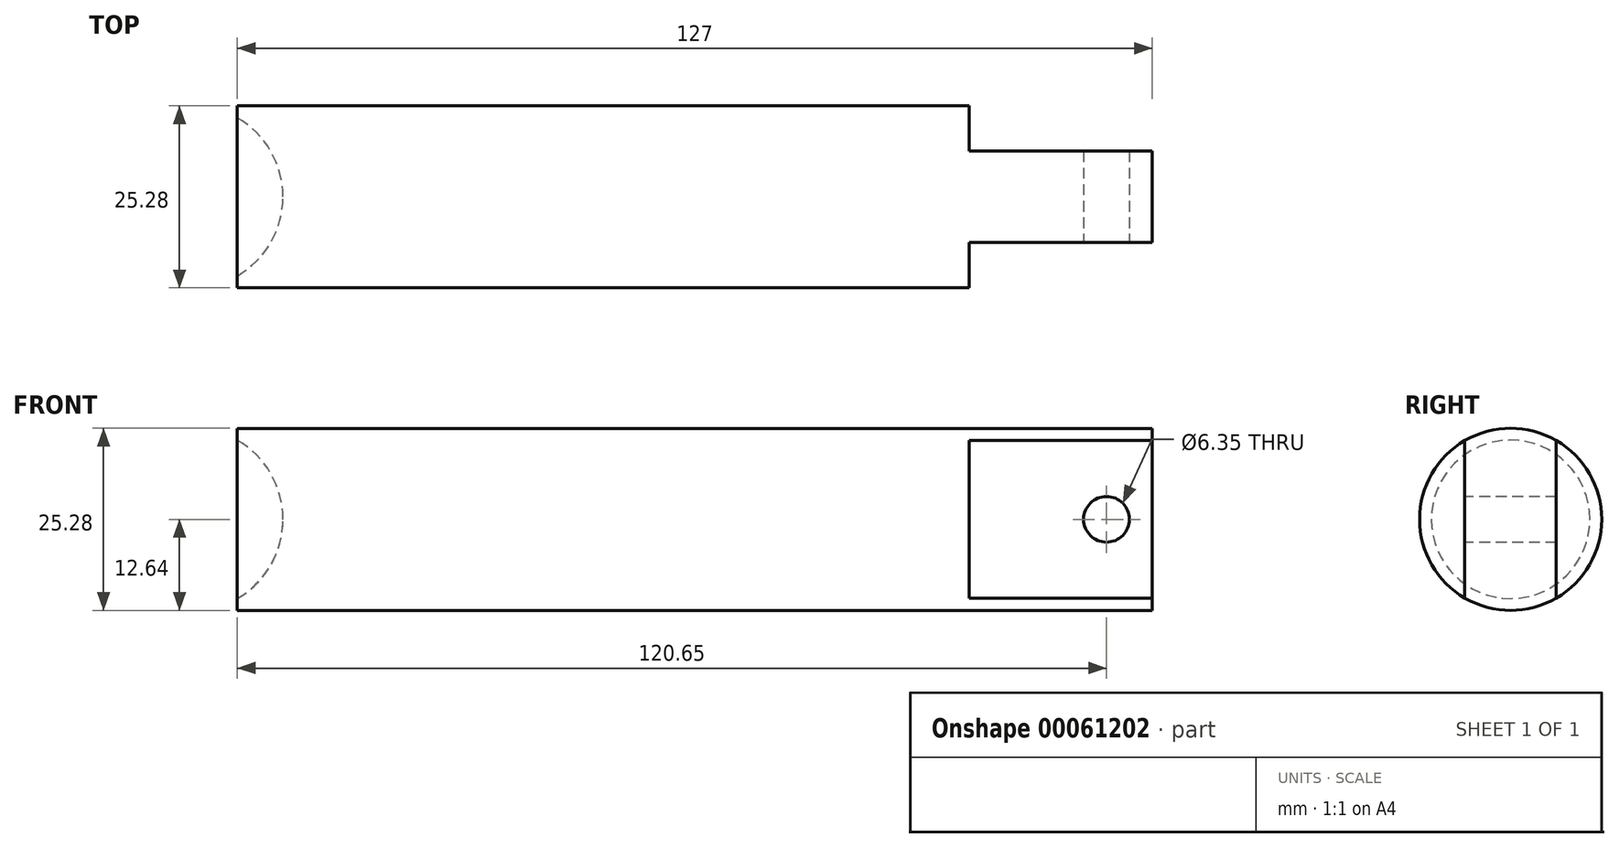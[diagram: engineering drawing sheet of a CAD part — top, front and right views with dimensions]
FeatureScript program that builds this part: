
annotation { "Feature Type Name" : "Feature", "Feature Type Description" : "" }
export const myFeature = defineFeature(function(context is Context, id is Id, definition is map)
    precondition{}
    {
        {
            var Q0;
            Q0=qCreatedBy(makeId("Right.planeOp"),FACE);
            var sketch = newSketch(context, id + "F0", { "sketchPlane" : qUnion([Q0])});
            skCircle(sketch, "E0", {"center": v(0, 0) * mm, "radius": 12.64 * mm});
            skSolve(sketch);
        }
        {
            var Q0;
            Q0=makeQuery(id+"F0.imprint","IMPRINT",FACE,{"disambiguationData":[TD([[makeQuery(id+"F0.imprint","IMPRINT",EDGE,{"derivedFrom":sQuery(id+"F0.wireOp",EDGE,"E0")}),1.0]])]});
            extrude(context, id + "F1", {"entities" : qUnion([Q0]), "endBound" : BoundingType.SYMMETRIC, "depth" : 127 * mm});
        }
        {
            var Q0;
            Q0=makeQuery(id+"F1.opExtrude","CAP_FACE",FACE,{"disambiguationData":[OSD([sQuery(id+"F0.wireOp",EDGE,"E0")])],"isStart":false});
            var sketch = newSketch(context, id + "F2", { "sketchPlane" : qUnion([Q0])});
            skLineSegment(sketch, "E1.bottom", {"start": v(36.51, -26.9) * mm, "end": v(6.35, -26.9) * mm});
            skLineSegment(sketch, "E1.top", {"start": v(36.51, 29.46) * mm, "end": v(6.35, 29.46) * mm});
            skLineSegment(sketch, "E1.left", {"start": v(36.51, -26.9) * mm, "end": v(36.51, 29.46) * mm});
            skLineSegment(sketch, "E1.right", {"start": v(6.35, -26.9) * mm, "end": v(6.35, 29.46) * mm});
            skLineSegment(sketch, "E2.bottom", {"start": v(-23.02, 30.25) * mm, "end": v(-6.35, 30.25) * mm});
            skLineSegment(sketch, "E2.top", {"start": v(-23.02, -29.67) * mm, "end": v(-6.35, -29.67) * mm});
            skLineSegment(sketch, "E2.left", {"start": v(-23.02, 30.25) * mm, "end": v(-23.02, -29.67) * mm});
            skLineSegment(sketch, "E2.right", {"start": v(-6.35, 30.25) * mm, "end": v(-6.35, -29.67) * mm});
            skSolve(sketch);
        }
        {
            var Q0;
            Q0 = qSketchRegion(id + "F2", true);
            extrude(context, id + "F3", {"entities" : qUnion([Q0]), "operationType" : NewBodyOperationType.REMOVE, "oppositeDirection" : true, "depth" : 25.4 * mm});
        }
        {
            var Q0;
            Q0=makeQuery(id+"F3.boolean.opBoolean","COPY",FACE,{"derivedFrom":makeQuery(id+"F3.opExtrude","SWEPT_FACE",FACE,{"disambiguationData":[OSD([sQuery(id+"F2.wireOp",EDGE,"E2.right")])]})});
            var sketch = newSketch(context, id + "F4", { "sketchPlane" : qUnion([Q0])});
            skCircle(sketch, "E3", {"center": v(57.15, 0) * mm, "radius": 3.18 * mm});
            skSolve(sketch);
        }
        {
            var Q0;
            Q0 = qSketchRegion(id + "F4", true);
            extrude(context, id + "F5", {"entities" : qUnion([Q0]), "operationType" : NewBodyOperationType.REMOVE, "oppositeDirection" : true, "depth" : 25.4 * mm});
        }
        {
            var Q0;
            Q0=qCreatedBy(makeId("Front.planeOp"),FACE);
            var sketch = newSketch(context, id + "F6", { "sketchPlane" : qUnion([Q0])});
            skArc(sketch, "E4", {"start": v(-57.15, 0) * mm, "mid": v(-58.85, 6.35) * mm, "end": v(-63.5, 11) * mm});
            skLineSegment(sketch, "E5", {"start": v(-63.5, 11) * mm, "end": v(-63.5, 0) * mm});
            skLineSegment(sketch, "E6", {"start": v(-63.5, 0) * mm, "end": v(-57.15, 0) * mm});
            skSolve(sketch);
        }
        {
            var Q0;
            Q0 = qSketchRegion(id + "F6", true);
            var Q1;
            Q1=sQuery(id+"F6.wireOp",EDGE,"E6");
            revolve(context, id + "F7", {"operationType" : NewBodyOperationType.REMOVE, "entities" : qUnion([Q0]), "axis" : qUnion([Q1]), "revolveType" : RevolveType.FULL, "oppositeDirection" : true});
        }
    });
